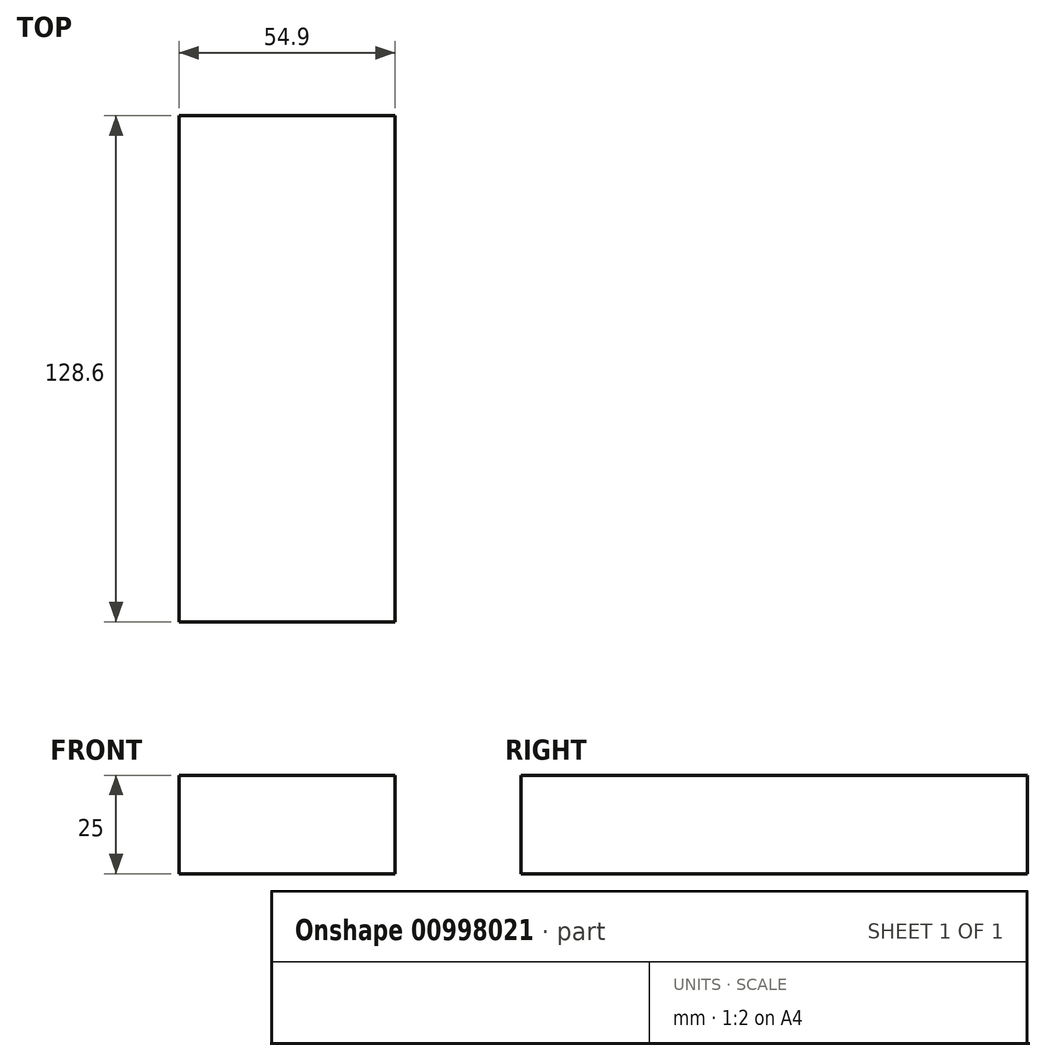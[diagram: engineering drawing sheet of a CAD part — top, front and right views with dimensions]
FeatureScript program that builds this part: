
annotation { "Feature Type Name" : "Feature", "Feature Type Description" : "" }
export const myFeature = defineFeature(function(context is Context, id is Id, definition is map)
    precondition{}
    {
        {
            var Q0;
            Q0=qCreatedBy(makeId("Top.planeOp"),FACE);
            var sketch = newSketch(context, id + "F0", { "sketchPlane" : qUnion([Q0])});
            skLineSegment(sketch, "E0.bottom", {"start": v(0, 0) * mm, "end": v(0, 0) * mm});
            skLineSegment(sketch, "E0.top", {"start": v(0, 51.1) * mm, "end": v(0, 51.1) * mm});
            skPoint(sketch, "E0.middle", {"position": v(0, 25.55) * mm});
            skPoint(sketch, "E1.middle", {"position": v(29, 51.1) * mm});
            skLineSegment(sketch, "E2.bottom", {"start": v(-10.96, 51.1) * mm, "end": v(43.94, 51.1) * mm});
            skLineSegment(sketch, "E2.top", {"start": v(-10.96, -77.5) * mm, "end": v(43.94, -77.5) * mm});
            skLineSegment(sketch, "E2.left", {"start": v(-10.96, 51.1) * mm, "end": v(-10.96, -77.5) * mm});
            skLineSegment(sketch, "E2.right", {"start": v(43.94, 51.1) * mm, "end": v(43.94, -77.5) * mm});
            skPoint(sketch, "E2.middle", {"position": v(16.5, -13.2) * mm});
            skPoint(sketch, "E2.middle.positionSnap0", {"position": v(16.5, 51.1) * mm});
            skPoint(sketch, "E2.cornerSnap0", {"position": v(16.5, 51.1) * mm});
            skPoint(sketch, "E2.centerSnap0", {"position": v(16.5, 51.1) * mm});
            skPoint(sketch, "E3.orphan", {"position": v(41.52, 76.65) * mm});
            skPoint(sketch, "E4.orphan", {"position": v(16.5, 76.65) * mm});
            skPoint(sketch, "E1.right.start.orphan", {"position": v(16.5, 25.55) * mm});
            skPoint(sketch, "E1.left.start.orphan", {"position": v(41.52, 25.55) * mm});
            skSolve(sketch);
        }
        {
            var Q0;
            Q0=makeQuery(id+"F0.imprint","IMPRINT",FACE,{"disambiguationData":[TD([[makeQuery(id+"F0.imprint","IMPRINT",EDGE,{"derivedFrom":sQuery(id+"F0.wireOp",EDGE,"E2.bottom")}),-1.0]])]});
            extrude(context, id + "F1", {"entities" : qUnion([Q0]), "depth" : 25 * mm, "offsetDistance" : 25 * mm});
        }
    });
